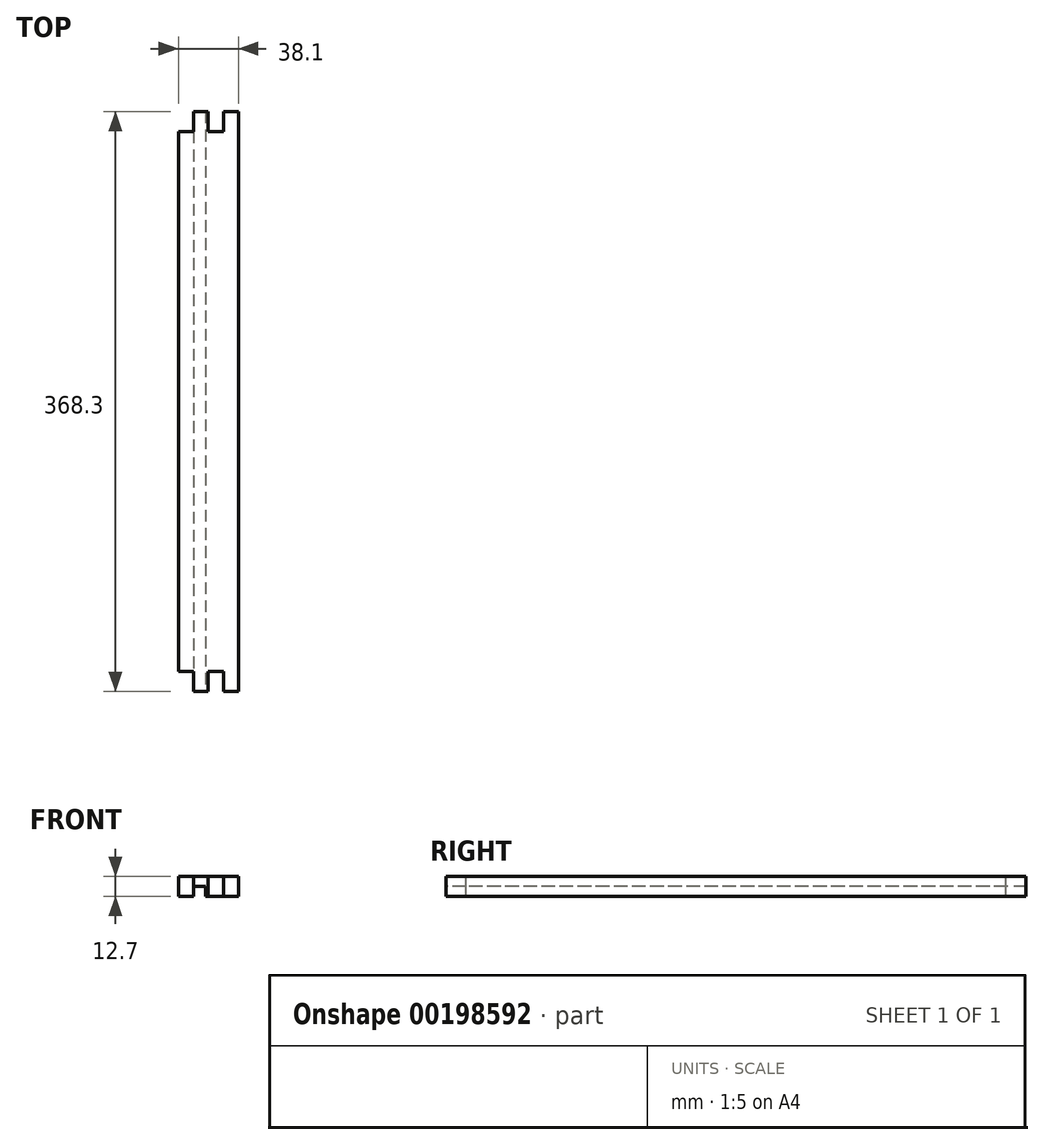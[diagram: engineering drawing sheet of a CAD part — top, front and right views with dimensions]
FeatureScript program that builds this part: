
annotation { "Feature Type Name" : "Feature", "Feature Type Description" : "" }
export const myFeature = defineFeature(function(context is Context, id is Id, definition is map)
    precondition{}
    {
        {
            var Q0;
            Q0=qCreatedBy(makeId("Front.planeOp"),FACE);
            var sketch = newSketch(context, id + "F0", { "sketchPlane" : qUnion([Q0])});
            skLineSegment(sketch, "E0.bottom", {"start": v(0, 0) * mm, "end": v(38.1, 0) * mm});
            skLineSegment(sketch, "E0.top", {"start": v(0, 12.7) * mm, "end": v(38.1, 12.7) * mm});
            skLineSegment(sketch, "E0.left", {"start": v(0, 0) * mm, "end": v(0, 12.7) * mm});
            skLineSegment(sketch, "E0.right", {"start": v(38.1, 0) * mm, "end": v(38.1, 12.7) * mm});
            skSolve(sketch);
        }
        {
            var Q0;
            Q0 = qSketchRegion(id + "F0", true);
            extrude(context, id + "F1", {"entities" : qUnion([Q0]), "depth" : 368.3 * mm});
        }
        {
            var Q0;
            Q0=makeQuery(id+"F1.opExtrude","CAP_FACE",FACE,{"disambiguationData":[OSD([sQuery(id+"F0.wireOp",EDGE,"E0.bottom"),sQuery(id+"F0.wireOp",EDGE,"E0.top"),sQuery(id+"F0.wireOp",EDGE,"E0.left"),sQuery(id+"F0.wireOp",EDGE,"E0.right")])],"isStart":false});
            var sketch = newSketch(context, id + "F2", { "sketchPlane" : qUnion([Q0])});
            skLineSegment(sketch, "E1", {"start": v(9.53, 0) * mm, "end": v(9.53, 6.35) * mm});
            skLineSegment(sketch, "E2", {"start": v(9.53, 6.35) * mm, "end": v(17.14, 6.35) * mm});
            skLineSegment(sketch, "E3", {"start": v(17.14, 6.35) * mm, "end": v(17.14, 0) * mm});
            skLineSegment(sketch, "E4", {"start": v(17.14, 0) * mm, "end": v(9.53, 0) * mm});
            skSolve(sketch);
        }
        {
            var Q0;
            Q0 = qSketchRegion(id + "F2", true);
            extrude(context, id + "F3", {"entities" : qUnion([Q0]), "operationType" : NewBodyOperationType.REMOVE, "endBound" : BoundingType.THROUGH_ALL, "oppositeDirection" : true, "depth" : 25.4 * mm});
        }
        {
            var Q0;
            Q0=makeQuery(id+"F1.opExtrude","SWEPT_FACE",FACE,{"disambiguationData":[OSD([sQuery(id+"F0.wireOp",EDGE,"E0.top")])]});
            var sketch = newSketch(context, id + "F4", { "sketchPlane" : qUnion([Q0])});
            skLineSegment(sketch, "E5", {"start": v(28.58, 0) * mm, "end": v(28.58, -12.7) * mm});
            skLineSegment(sketch, "E6", {"start": v(28.58, -12.7) * mm, "end": v(19.05, -12.7) * mm});
            skLineSegment(sketch, "E7", {"start": v(19.05, -12.7) * mm, "end": v(19.05, 0) * mm});
            skLineSegment(sketch, "E8", {"start": v(19.05, 0) * mm, "end": v(28.58, 0) * mm});
            skLineSegment(sketch, "E9", {"start": v(9.53, 0) * mm, "end": v(9.53, -12.7) * mm});
            skLineSegment(sketch, "E10", {"start": v(9.53, -12.7) * mm, "end": v(0, -12.7) * mm});
            skLineSegment(sketch, "E11", {"start": v(0, -12.7) * mm, "end": v(0, 0) * mm});
            skLineSegment(sketch, "E12", {"start": v(0, 0) * mm, "end": v(9.53, 0) * mm});
            skPoint(sketch, "E13.endSnap0", {"position": v(0, -184.15) * mm});
            skLineSegment(sketch, "E14.MirrorCS", {"start": v(0, -368.3) * mm, "end": v(9.53, -368.3) * mm});
            skLineSegment(sketch, "E15.MirrorCS", {"start": v(19.05, -368.3) * mm, "end": v(28.58, -368.3) * mm});
            skLineSegment(sketch, "E16.MirrorCS", {"start": v(9.53, -355.6) * mm, "end": v(0, -355.6) * mm});
            skLineSegment(sketch, "E17.MirrorCS", {"start": v(28.58, -355.6) * mm, "end": v(19.05, -355.6) * mm});
            skLineSegment(sketch, "E18.MirrorCS", {"start": v(19.05, -355.6) * mm, "end": v(19.05, -368.3) * mm});
            skLineSegment(sketch, "E19.MirrorCS", {"start": v(9.53, -368.3) * mm, "end": v(9.53, -355.6) * mm});
            skLineSegment(sketch, "E20.MirrorCS", {"start": v(28.58, -368.3) * mm, "end": v(28.58, -355.6) * mm});
            skLineSegment(sketch, "E21.MirrorCS", {"start": v(0, -355.6) * mm, "end": v(0, -368.3) * mm});
            skSolve(sketch);
        }
        {
            var Q0;
            Q0 = qSketchRegion(id + "F4", true);
            extrude(context, id + "F5", {"entities" : qUnion([Q0]), "operationType" : NewBodyOperationType.REMOVE, "oppositeDirection" : true, "depth" : 25.4 * mm});
        }
    });
